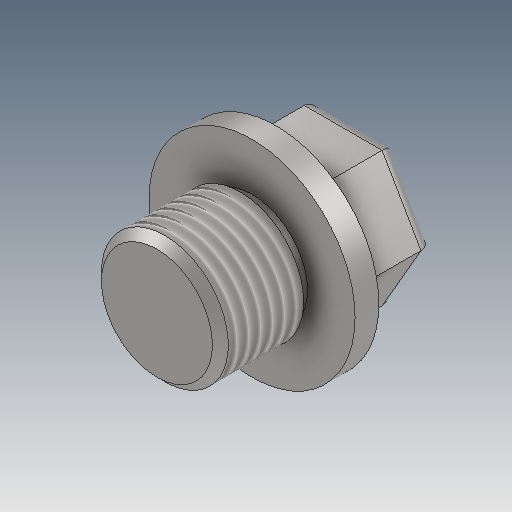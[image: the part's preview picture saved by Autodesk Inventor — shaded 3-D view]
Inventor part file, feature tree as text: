
AUTODESK INVENTOR PART (.ipt)
format: ipt  version: 2025 (Build 290162000, 162)  size: 361,472 bytes
history: native  units: mm
features: sketch x2, revolve x1, chamfer x1, thread x1, extrude x1, fillet x1
ambient origin geometry x8: Origin, YZ Plane, XZ Plane, XY Plane, X Axis, Y Axis, Z Axis, Center Point
bodies: 实体1 (feature_tree)
feature tree (7):
  revolve  "旋转1"  [1 undecoded]
  chamfer  "倒角1"  Distance=1.5mm
  thread  "螺纹1"  [1 undecoded]
  extrude  "拉伸1"  Depth=8.0mm
  fillet  "圆角1"  Radius=12.0mm
  sketch  "草图1"  dims[d1=17.0mm d0=13.0mm]
  sketch  "草图2"  dims[d2=3.0mm d3=1.5mm d4=1.0mm d5=8.0mm d6=12.0mm d7=90.0deg d8=1.0mm d9=2.0mm d10=45.0deg d11=20.0mm d12=0.0mm d13=17.0mm d14=10.0mm d15=0.0mm d16=1.5mm]
note: 2 required parameter values undecoded (feature->parameter linkage not recoverable at this tier; creation-order binding heuristic only, values carry confidence <= 0.55)